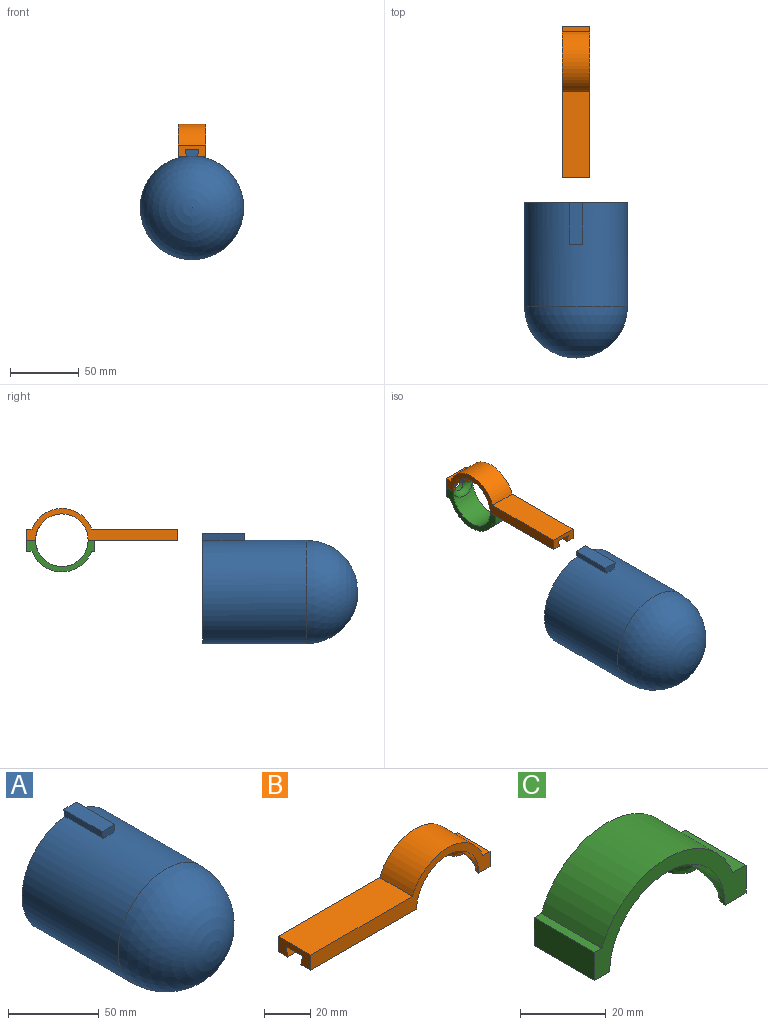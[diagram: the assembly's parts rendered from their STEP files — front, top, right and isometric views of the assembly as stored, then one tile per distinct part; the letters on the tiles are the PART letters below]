
ASSEMBLY  parts=3 mates=2
PART A: 9 faces, bbox 75x112.5x80 mm
  f0: sphere r=37.5mm, area 8835.7mm2, adj f1
  f1: cylinder r=37.5mm len=75mm, axis (0,-1,0), area 17431mm2, adj f0,f2,f5,f7,f8
  f2: plane 80x75mm, normal (0,1,0), area 324mm2, adj f1,f3,f5,f6,f7
  f3: cylinder r=36.3mm len=75mm, axis (0,-1,0), area 17106mm2, adj f2,f4
  f4: sphere r=36.3mm, area 8279.3mm2, adj f3
  f5: plane 30x5.21mm, normal (-0.98,0,-0.19), area 159.3mm2, adj f1,f2,f6,f8
  f6: plane 30x10mm, normal (0,0,1), area 300mm2, adj f2,f5,f7,f8
  f7: plane 30x5.21mm, normal (0.98,0,-0.19), area 159.3mm2, adj f1,f2,f6,f8
  f8: plane 10x5.21mm, normal (0,-1,0), area 45.8mm2, adj f1,f5,f6,f7
PART B: 17 faces, bbox 110x20x23.6 mm
  f0: plane 20x8mm, normal (-1,0,0), area 115mm2, adj f1,f2,f3,f4,f6,f7,f8
  f1: plane 110x23.05mm, normal (0,1,0), area 783.3mm2, adj f0,f2,f3,f5,f10,f11,f13,f16
  f2: plane 65x20mm, normal (0,0,-1), area 1060mm2, adj f0,f1,f4,f5,f6,f7,f9
  f3: plane 62.43x20mm, normal (0,0,1), area 1248.7mm2, adj f0,f1,f4,f16
  f4: plane 110x23.05mm, normal (0,-1,0), area 783.3mm2, adj f0,f2,f3,f5,f10,f12,f13,f16
  f5: cylinder r=19.05mm len=38.1mm, axis (0,-1,0), area 1069.7mm2, adj f1,f2,f4,f15
  f6: plane 30x5mm, normal (0,-0.98,0.2), area 153mm2, adj f0,f2,f8,f9
  f7: plane 30x5mm, normal (0,0.98,0.2), area 153mm2, adj f0,f2,f8,f9
  f8: plane 30x10mm, normal (0,0,-1), area 300mm2, adj f0,f6,f7,f9
  f9: plane 10x5mm, normal (-1,0,0), area 45mm2, adj f2,f6,f7,f8
  f10: plane 20x4.33mm, normal (0,0,1), area 86.7mm2, adj f1,f4,f13,f16
  f11: plane 6.9x5mm, normal (0,0,-1), area 29.1mm2, adj f1,f13,f14,f15
  f12: plane 6.9x5mm, normal (0,0,-1), area 29.1mm2, adj f4,f13,f14,f15
  f13: plane 20x8mm, normal (1,0,0), area 120.7mm2, adj f1,f4,f10,f11,f12,f14
  f14: cylinder r=5mm len=10mm, axis (1,0,0), area 46.7mm2, adj f11,f12,f13,f15
  f15: bspline ~20.01x8.46mm, area 137.4mm2, adj f5,f11,f12,f14
  f16: cylinder r=23.05mm len=43.23mm, axis (0,-1,0), area 1121.5mm2, adj f1,f3,f4,f10
PART C: 13 faces, bbox 50x20x23.6 mm
  f0: plane 20x8mm, normal (-1,0,0), area 160mm2, adj f1,f2,f3,f4
  f1: plane 50x23.05mm, normal (0,1,0), area 303.3mm2, adj f0,f2,f3,f5,f6,f7,f9,f12
  f2: plane 20x5mm, normal (0,0,-1), area 100mm2, adj f0,f1,f4,f5
  f3: plane 20x2.43mm, normal (0,0,1), area 48.7mm2, adj f0,f1,f4,f12
  f4: plane 50x23.05mm, normal (0,-1,0), area 303.3mm2, adj f0,f2,f3,f5,f6,f8,f9,f12
  f5: cylinder r=19.05mm len=38.1mm, axis (0,-1,0), area 1069.7mm2, adj f1,f2,f4,f11
  f6: plane 20x4.33mm, normal (0,0,1), area 86.7mm2, adj f1,f4,f9,f12
  f7: plane 6.9x5mm, normal (0,0,-1), area 29.1mm2, adj f1,f9,f10,f11
  f8: plane 6.9x5mm, normal (0,0,-1), area 29.1mm2, adj f4,f9,f10,f11
  f9: plane 20x8mm, normal (1,0,0), area 120.7mm2, adj f1,f4,f6,f7,f8,f10
  f10: cylinder r=5mm len=10mm, axis (1,0,0), area 46.7mm2, adj f7,f8,f9,f11
  f11: bspline ~20.01x8.46mm, area 137.4mm2, adj f5,f7,f8,f10
  f12: cylinder r=23.05mm len=43.23mm, axis (0,-1,0), area 1121.5mm2, adj f1,f3,f4,f6
PLACE A t=(0,37.5,0)mm
PLACE B rot(axis=(0,0,1),90deg) t=(0,155.72,37.5)mm
PLACE C rot(axis=(0.71,0.71,0),180deg) t=(0,155.72,37.5)mm
MATE slider B.f0 <-> A.f8  axis (0,-1,0) through (0,55.72,42.5)mm
MATE fastened C.f9 <-> B.f13  axis (0,1,0) through (7.5,165.72,37.5)mm
